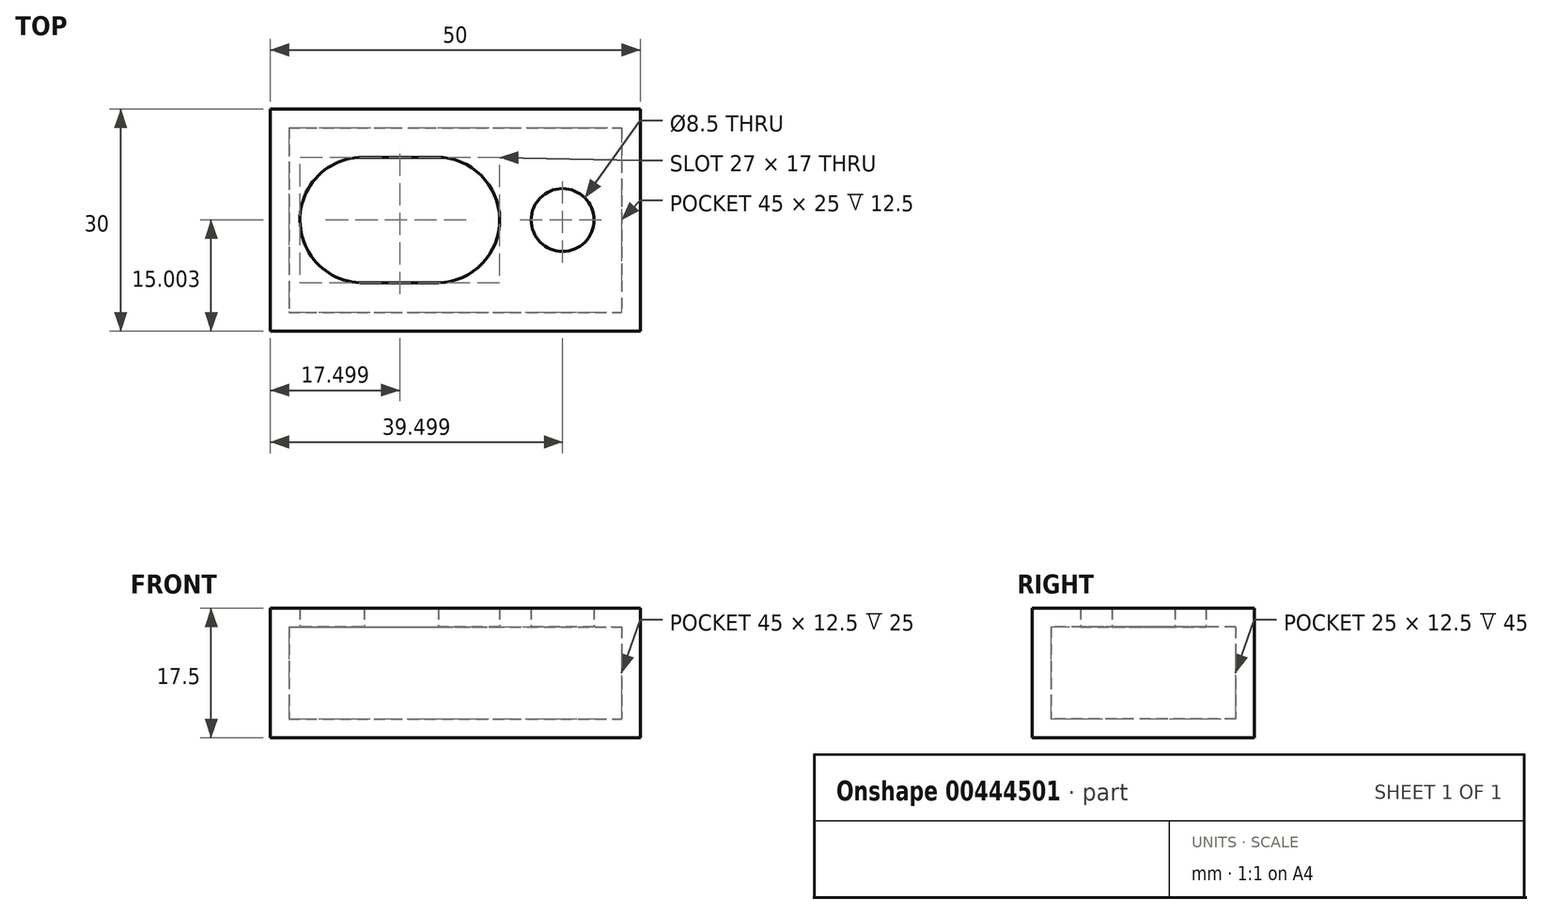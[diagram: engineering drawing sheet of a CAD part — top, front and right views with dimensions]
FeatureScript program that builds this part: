
annotation { "Feature Type Name" : "Feature", "Feature Type Description" : "" }
export const myFeature = defineFeature(function(context is Context, id is Id, definition is map)
    precondition{}
    {
        {
            var Q0;
            Q0=qCreatedBy(makeId("Top.planeOp"),FACE);
            var sketch = newSketch(context, id + "F0", { "sketchPlane" : qUnion([Q0])});
            skLineSegment(sketch, "E0.bottom", {"start": v(-34.94, 21.44) * mm, "end": v(15.06, 21.44) * mm});
            skLineSegment(sketch, "E0.top", {"start": v(-34.94, -8.56) * mm, "end": v(15.06, -8.56) * mm});
            skLineSegment(sketch, "E0.left", {"start": v(-34.94, 21.44) * mm, "end": v(-34.94, -8.56) * mm});
            skLineSegment(sketch, "E0.right", {"start": v(15.06, 21.44) * mm, "end": v(15.06, -8.56) * mm});
            skSolve(sketch);
        }
        {
            var Q0;
            Q0=makeQuery(id+"F0.imprint","IMPRINT",FACE,{"disambiguationData":[TD([[makeQuery(id+"F0.imprint","IMPRINT",EDGE,{"derivedFrom":sQuery(id+"F0.wireOp",EDGE,"E0.bottom")}),-1.0]])]});
            extrude(context, id + "F1", {"entities" : qUnion([Q0]), "depth" : 15 * mm});
        }
        {
            var Q0;
            Q0=makeQuery(id+"F1.opExtrude","CAP_FACE",FACE,{"disambiguationData":[OSD([sQuery(id+"F0.wireOp",EDGE,"E0.bottom"),sQuery(id+"F0.wireOp",EDGE,"E0.top"),sQuery(id+"F0.wireOp",EDGE,"E0.left"),sQuery(id+"F0.wireOp",EDGE,"E0.right")])],"isStart":false});
            shell(context, id + "F2", {"entities" : qUnion([Q0]), "thickness" : 2.5 * mm});
        }
        {
            var Q0;
            Q0=makeQuery(id+"F1.opExtrude","CAP_FACE",FACE,{"disambiguationData":[OSD([sQuery(id+"F0.wireOp",EDGE,"E0.bottom"),sQuery(id+"F0.wireOp",EDGE,"E0.top"),sQuery(id+"F0.wireOp",EDGE,"E0.left"),sQuery(id+"F0.wireOp",EDGE,"E0.right")])],"isStart":false});
            var sketch = newSketch(context, id + "F3", { "sketchPlane" : qUnion([Q0])});
            skLineSegment(sketch, "E1.bottom", {"start": v(-34.94, 21.44) * mm, "end": v(15.06, 21.44) * mm});
            skLineSegment(sketch, "E1.top", {"start": v(-34.94, -8.56) * mm, "end": v(15.06, -8.56) * mm});
            skLineSegment(sketch, "E1.left", {"start": v(-34.94, 21.44) * mm, "end": v(-34.94, -8.56) * mm});
            skLineSegment(sketch, "E1.right", {"start": v(15.06, 21.44) * mm, "end": v(15.06, -8.56) * mm});
            skLineSegment(sketch, "E2", {"start": v(-22.44, 14.94) * mm, "end": v(-12.44, 14.94) * mm});
            skLineSegment(sketch, "E3", {"start": v(-22.25, -2.06) * mm, "end": v(-12.25, -2.06) * mm});
            skArc(sketch, "E4", {"start": v(-22.44, 14.94) * mm, "mid": v(-30.94, 6.34) * mm, "end": v(-22.25, -2.06) * mm});
            skArc(sketch, "E5", {"start": v(-12.44, 14.94) * mm, "mid": v(-3.94, 6.54) * mm, "end": v(-12.25, -2.06) * mm});
            skCircle(sketch, "E6", {"center": v(4.56, 6.44) * mm, "radius": 4.25 * mm});
            skSolve(sketch);
        }
        {
            var Q0;
            Q0 = qSketchRegion(id + "F3", true);
            extrude(context, id + "F4", {"entities" : qUnion([Q0]), "operationType" : NewBodyOperationType.ADD, "depth" : 2.5 * mm});
        }
    });
